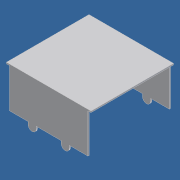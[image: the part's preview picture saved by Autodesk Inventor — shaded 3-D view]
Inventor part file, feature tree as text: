
AUTODESK INVENTOR PART (.ipt)
format: ipt  version: 2014 (Build 180170000, 170)  size: 109,056 bytes
history: native  units: in
note: dims shown in document units (in); Inventor stores cm internally (conversion verified against a paired STEP export)
features: other x7, extrude x3, sketch x3
ambient origin geometry x8: Origin, YZ Plane, XZ Plane, XY Plane, X Axis, Y Axis, Z Axis, Center Point
bodies: Solid1 (feature_tree)
feature tree (13):
  extrude  "Extrusion1"  Depth=0.008in TaperAngle=0.0deg
  extrude  "Extrusion2"  [1 undecoded]
  extrude  "Extrusion3"  [1 undecoded]
  other  "shroud_to_body_XY"
  other  "shroud_to_body_YZ"
  other  "shroud_to_body_ZX"
  other  "shroud_to_body_X"
  other  "shroud_to_body_Y"
  other  "shroud_to_body_Z"
  other  "shroud_to_body_Center"
  sketch  "Sketch_1"  dims[d0=0.008in d1=0.0in d2=0.008in d3=0.0in]
  sketch  "Sketch_2"  dims[d4=0.008in d5=0.0in]
  sketch  "Sketch_3"
note: 2 required parameter values undecoded (feature->parameter linkage not recoverable at this tier; creation-order binding heuristic only, values carry confidence <= 0.55)
